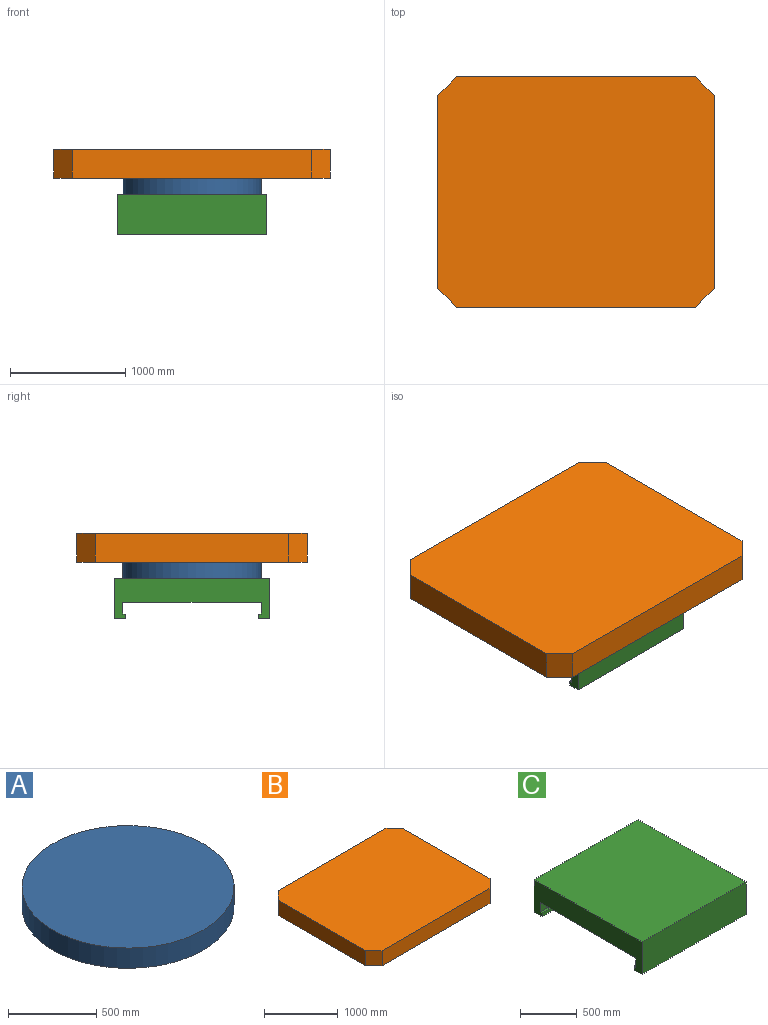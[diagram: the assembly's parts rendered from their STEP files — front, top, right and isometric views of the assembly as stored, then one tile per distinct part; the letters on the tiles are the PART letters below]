
ASSEMBLY  parts=3 mates=2
PART A: 3 faces, bbox 1200x1200x140 mm
  f0: cylinder r=600mm len=1200mm, axis (0,0,-1), area 527787.6mm2, adj f1,f2
  f1: plane 1200x1200mm, normal (0,0,1), area 1130973.4mm2, adj f0
  f2: plane 1200x1200mm, normal (0,0,-1), area 1130973.4mm2, adj f0
PART B: 10 faces, bbox 2400x2000x250 mm
  f0: plane 1676x250mm, normal (1,0,0), area 419000mm2, adj f4,f5,f8,f9
  f1: plane 2076x250mm, normal (0,1,0), area 519000mm2, adj f4,f5,f7,f8
  f2: plane 1676x250mm, normal (-1,0,0), area 419000mm2, adj f4,f5,f6,f7
  f3: plane 2076x250mm, normal (0,-1,0), area 519000mm2, adj f4,f5,f6,f9
  f4: plane 2400x2000mm, normal (0,0,1), area 4747512mm2, adj f0,f1,f2,f3,f6,f7,f8,f9
  f5: plane 2400x2000mm, normal (0,0,-1), area 4747512mm2, adj f0,f1,f2,f3,f6,f7,f8,f9
  f6: plane 250x162mm, normal (-0.71,-0.71,0), area 57275.6mm2, adj f2,f3,f4,f5
  f7: plane 250x162mm, normal (-0.71,0.71,0), area 57275.6mm2, adj f1,f2,f4,f5
  f8: plane 250x162mm, normal (0.71,0.71,0), area 57275.6mm2, adj f0,f1,f4,f5
  f9: plane 250x162mm, normal (0.71,-0.71,0), area 57275.6mm2, adj f0,f3,f4,f5
PART C: 14 faces, bbox 1300x1350x350 mm
  f0: plane 1350x1300mm, normal (0,0,1), area 1755000mm2, adj f1,f11,f12,f13
  f1: plane 1300x350mm, normal (0,-1,0), area 455000mm2, adj f0,f2,f12,f13
  f2: plane 1300x100mm, normal (0,0,-1), area 130000mm2, adj f1,f3,f12,f13
  f3: plane 1300x40mm, normal (0,1,0), area 52000mm2, adj f2,f4,f12,f13
  f4: plane 1300x25mm, normal (0,0,1), area 32500mm2, adj f3,f5,f12,f13
  f5: plane 1300x100mm, normal (0,1,0), area 130000mm2, adj f4,f6,f12,f13
  f6: plane 1300x1200mm, normal (0,0,-1), area 1560000mm2, adj f5,f7,f12,f13
  f7: plane 1300x100mm, normal (0,-1,0), area 130000mm2, adj f6,f8,f12,f13
  f8: plane 1300x25mm, normal (0,0,1), area 32500mm2, adj f7,f9,f12,f13
  f9: plane 1300x40mm, normal (0,-1,0), area 52000mm2, adj f8,f10,f12,f13
  f10: plane 1300x100mm, normal (0,0,-1), area 130000mm2, adj f9,f11,f12,f13
  f11: plane 1300x350mm, normal (0,1,0), area 455000mm2, adj f0,f10,f12,f13
  f12: plane 1350x350mm, normal (-1,0,0), area 306500mm2, adj f0,f1,f2,f3,f4,f5,f6,f7
  f13: plane 1350x350mm, normal (1,0,0), area 306500mm2, adj f0,f1,f2,f3,f4,f5,f6,f7
PLACE A t=(1485.13,-2.06,291.56)mm
PLACE B rot(axis=(0,0,1),180deg) t=(2350.53,3265.34,431.56)mm
PLACE C t=(1549.37,2009.5,291.56)mm
MATE fastened C.f0 <-> A.f0  axis (0,0,1) through (899.37,2585.77,326.23)mm
MATE revolute B.f5 <-> A.f0  axis (0,0,-1) through (899.37,2585.77,466.23)mm
